# Revit family: MAGELLAN-DOWN_LIGHT_LED_19W_O185+connect_19_4000K
name_source: partatom
category: Lighting Fixtures
units: mm (PartAtom-declared; Revit-internal decimal feet)

## family parameters
Always vertical = Yes
Cut with Voids When Loaded = No
Host = Ceiling
Light Source = Yes
OmniClass Number = 23.80.70.11
OmniClass Title = Luminaries for Internal Lighting
Part Type = Normal
Room Calculation Point = No
Round Connector Dimension = Use Diameter
Shared = No

## types (1)
- Type 1
    Alimentation Driver = AC 220-240V
    Alimentation luminaire = 25-40V dc / 450mA
    Angle d'éclairage = 80°
    Color Filter = 16777215
    Couleur = Blanc
    Default Elevation = 0 mm  [stored 0 ft]
    Dimension découpe = Ø 165 mm
    Dimensions = Ø 185 mm, H = 93 mm
    Dimming Lamp Color Temperature Shift = <None>
    Driver = Driver Lifud TUV CE RCM CCC
    Durée de vie = 50 000 heures
    IRC = >90
    Lamp = LED Hongli 2835
    Maintien du flux = L80B10 (50 000 heures)
    Manufacturer = Lucera - Lucera (c) 06/01/2021 16:40:01 +01:00
    Matériau = Aluminium + PC réflecteur finition chrome
    Photometric Web File = google_eulumdat_converter.ies
    Puissance nominale = 19W
    SDCM = 3
    Tilt Angle = 90.00°
    URL = https://www.lucera.fr

note: [stored X ft] marks values corroborated as IEEE doubles in the binary element streams (Revit-internal decimal feet)

## geometry (parser evidence)
native form markers: Sweep x2
no freeform markers — native parametric forms only
